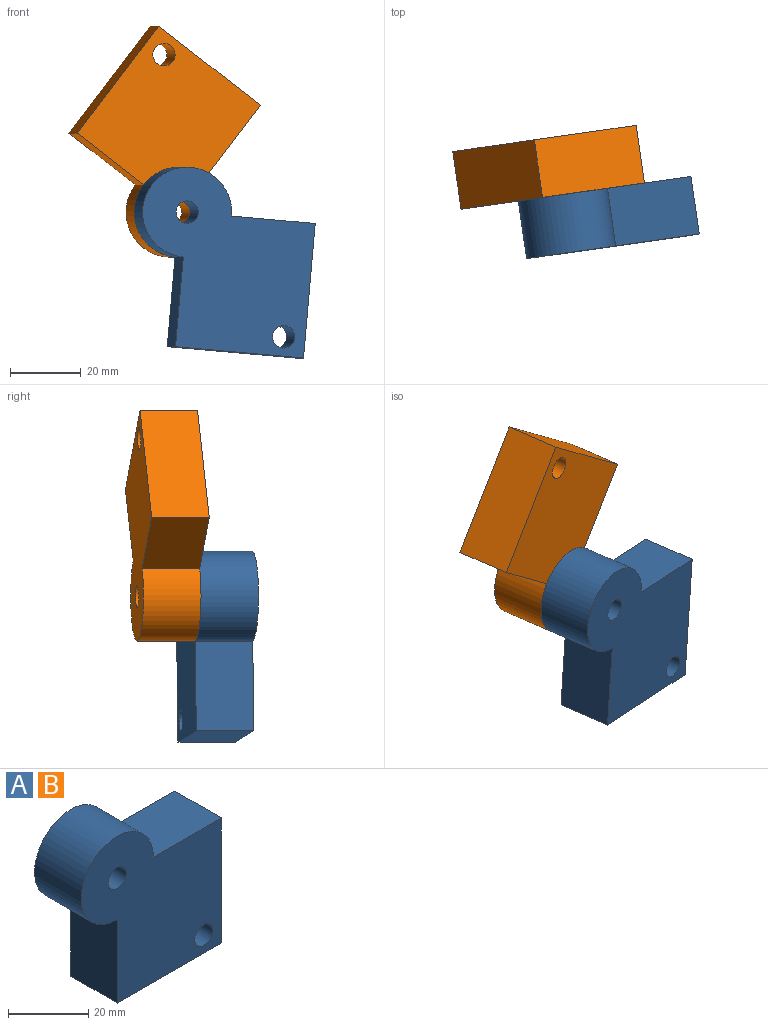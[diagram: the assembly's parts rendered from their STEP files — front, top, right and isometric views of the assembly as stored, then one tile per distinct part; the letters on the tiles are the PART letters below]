
ASSEMBLY  parts=2 mates=1
PART A: 9 faces, bbox 49.3x16.4x50.8 mm
  f0: plane 36.64x16.4mm, normal (0,0,-1), area 600.9mm2, adj f1,f4,f5,f6
  f1: plane 38.1x16.4mm, normal (1,0,0), area 624.8mm2, adj f0,f2,f5,f6
  f2: plane 23.94x16.4mm, normal (0,0,1), area 392.6mm2, adj f1,f3,f5,f6
  f3: cylinder r=12.7mm len=25.4mm, axis (0,1,0), area 981.5mm2, adj f2,f4,f5,f6
  f4: plane 25.4x16.4mm, normal (-1,0,0), area 416.6mm2, adj f0,f3,f5,f6
  f5: plane 50.8x49.34mm, normal (0,-1,0), area 1712.7mm2, adj f0,f1,f2,f3,f4,f7,f8
  f6: plane 50.8x49.34mm, normal (0,1,0), area 1712.7mm2, adj f0,f1,f2,f3,f4,f7,f8
  f7: cylinder r=3.17mm len=16.4mm, axis (0,-1,0), area 327.2mm2, adj f5,f6
  f8: cylinder r=3.17mm len=16.4mm, axis (0,-1,0), area 327.2mm2, adj f5,f6
PART B: same geometry as A
PLACE A rot(axis=(-0.04,0.52,0.85),9.6deg) t=(17.06,-66.68,183.33)mm
PLACE B rot(axis=(0.07,-1,0.02),142.5deg) t=(41.02,-46.68,251.48)mm
MATE revolute B.f3 <-> A.f3  axis (0.14,-0.99,0) through (20.35,-66.21,221.28)mm
